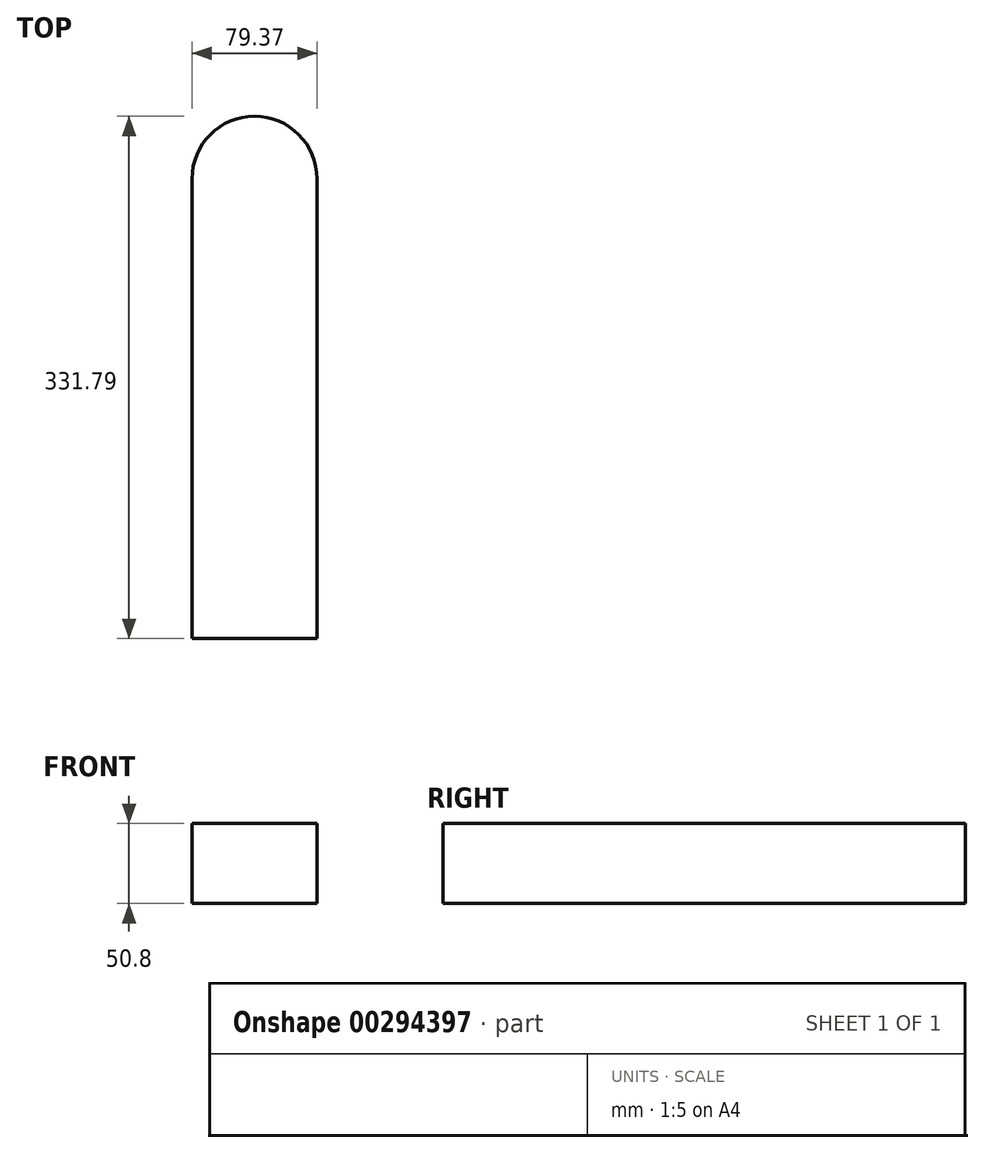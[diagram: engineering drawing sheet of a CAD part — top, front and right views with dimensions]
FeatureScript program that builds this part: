
annotation { "Feature Type Name" : "Feature", "Feature Type Description" : "" }
export const myFeature = defineFeature(function(context is Context, id is Id, definition is map)
    precondition{}
    {
        {
            var Q0;
            Q0=qCreatedBy(makeId("Top.planeOp"),FACE);
            var sketch = newSketch(context, id + "F0", { "sketchPlane" : qUnion([Q0])});
            skLineSegment(sketch, "E0.top", {"start": v(-55.2, -209.57) * mm, "end": v(24.18, -209.57) * mm});
            skLineSegment(sketch, "E0.left", {"start": v(-55.2, 82.53) * mm, "end": v(-55.2, -209.57) * mm});
            skLineSegment(sketch, "E0.right", {"start": v(24.18, 82.53) * mm, "end": v(24.18, -209.57) * mm});
            skArc(sketch, "E1", {"start": v(24.18, 82.53) * mm, "mid": v(-15.5, 122.22) * mm, "end": v(-55.2, 82.53) * mm});
            skSolve(sketch);
        }
        {
            var Q0;
            Q0 = qSketchRegion(id + "F0", true);
            extrude(context, id + "F1", {"entities" : qUnion([Q0]), "depth" : 50.8 * mm, "offsetDistance" : 25.4 * mm});
        }
    });
